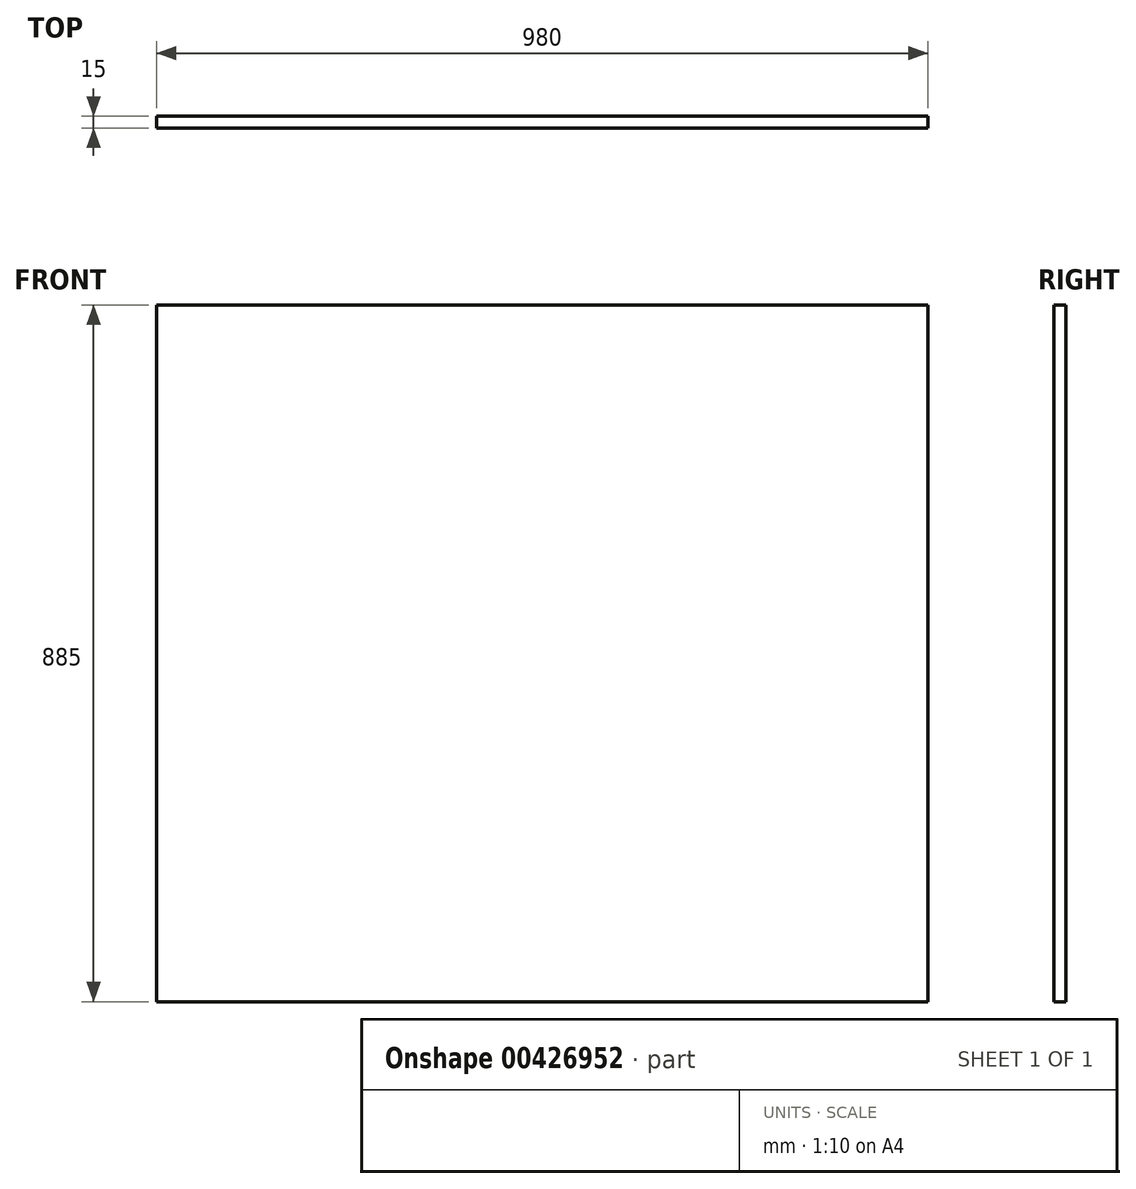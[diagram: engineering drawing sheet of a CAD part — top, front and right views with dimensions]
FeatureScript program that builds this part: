
annotation { "Feature Type Name" : "Feature", "Feature Type Description" : "" }
export const myFeature = defineFeature(function(context is Context, id is Id, definition is map)
    precondition{}
    {
        {
            var Q0;
            Q0=qCreatedBy(makeId("Front.planeOp"),FACE);
            var sketch = newSketch(context, id + "F0", { "sketchPlane" : qUnion([Q0])});
            skLineSegment(sketch, "E0.bottom", {"start": v(-524.72, 171.03) * mm, "end": v(455.28, 171.03) * mm});
            skLineSegment(sketch, "E0.top", {"start": v(-524.72, -713.97) * mm, "end": v(455.28, -713.97) * mm});
            skLineSegment(sketch, "E0.left", {"start": v(-524.72, 171.03) * mm, "end": v(-524.72, -713.97) * mm});
            skLineSegment(sketch, "E0.right", {"start": v(455.28, 171.03) * mm, "end": v(455.28, -713.97) * mm});
            skSolve(sketch);
        }
        {
            var Q0;
            Q0=makeQuery(id+"F0.imprint","IMPRINT",FACE,{"disambiguationData":[TD([[makeQuery(id+"F0.imprint","IMPRINT",EDGE,{"derivedFrom":sQuery(id+"F0.wireOp",EDGE,"E0.bottom")}),-1.0]])]});
            extrude(context, id + "F1", {"entities" : qUnion([Q0]), "depth" : 15 * mm});
        }
    });
